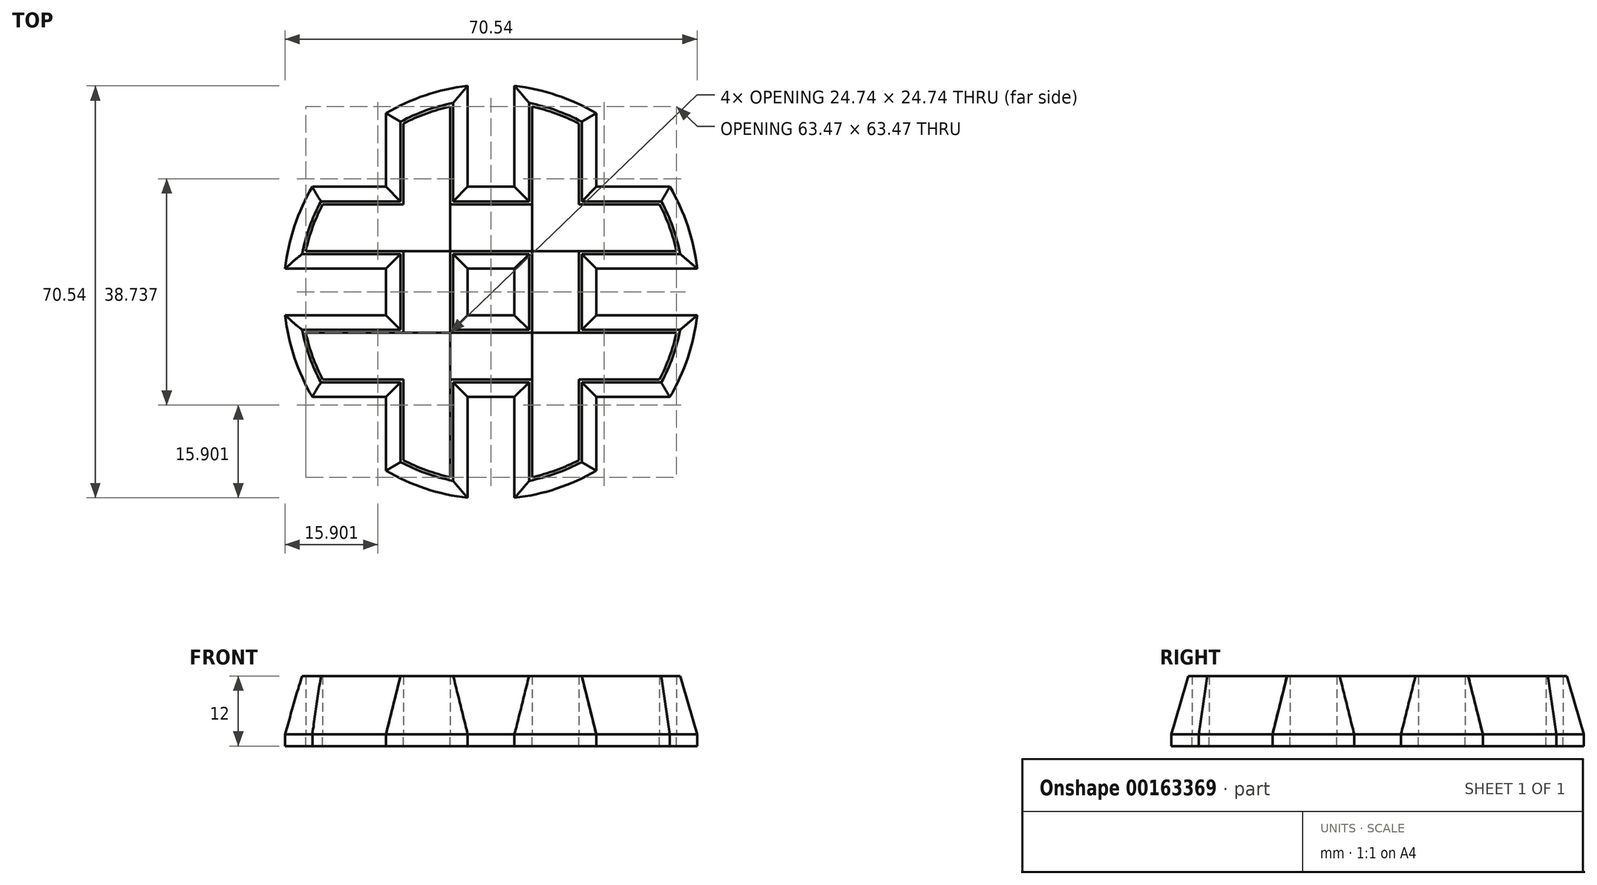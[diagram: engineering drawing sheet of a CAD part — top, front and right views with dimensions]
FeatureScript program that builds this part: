
annotation { "Feature Type Name" : "Feature", "Feature Type Description" : "" }
export const myFeature = defineFeature(function(context is Context, id is Id, definition is map)
    precondition{}
    {
        {
            var Q0;
            Q0=qCreatedBy(makeId("Top.planeOp"),FACE);
            var sketch = newSketch(context, id + "F0", { "sketchPlane" : qUnion([Q0])});
            skArc(sketch, "E0", {"start": v(-28.83, 15) * mm, "mid": v(-30.55, 11.1) * mm, "end": v(-31.74, 7) * mm});
            skLineSegment(sketch, "E1", {"start": v(-28.83, 15) * mm, "end": v(-15, 15) * mm});
            skLineSegment(sketch, "E2", {"start": v(-31.74, 7) * mm, "end": v(-15, 7) * mm});
            skLineSegment(sketch, "E3", {"start": v(-28.83, -15) * mm, "end": v(-15, -15) * mm});
            skLineSegment(sketch, "E4", {"start": v(31.74, -7) * mm, "end": v(15, -7) * mm});
            skLineSegment(sketch, "E5", {"start": v(15, 28.83) * mm, "end": v(15, 15) * mm});
            skLineSegment(sketch, "E6", {"start": v(7, -31.74) * mm, "end": v(7, -15) * mm});
            skLineSegment(sketch, "E7", {"start": v(-15, 28.83) * mm, "end": v(-15, 15) * mm});
            skLineSegment(sketch, "E8", {"start": v(-7, 31.74) * mm, "end": v(-7, 15) * mm});
            skArc(sketch, "E9.trimOffspring", {"start": v(15, 28.83) * mm, "mid": v(11.1, 30.55) * mm, "end": v(7, 31.74) * mm});
            skArc(sketch, "E10.trimOffspring", {"start": v(-31.74, -7) * mm, "mid": v(-30.55, -11.1) * mm, "end": v(-28.83, -15) * mm});
            skArc(sketch, "E11.trimOffspring", {"start": v(-15, -28.83) * mm, "mid": v(-11.1, -30.55) * mm, "end": v(-7, -31.74) * mm});
            skArc(sketch, "E12.trimOffspring", {"start": v(7, -31.74) * mm, "mid": v(11.1, -30.55) * mm, "end": v(15, -28.83) * mm});
            skArc(sketch, "E13.trimOffspring", {"start": v(28.83, -15) * mm, "mid": v(30.55, -11.1) * mm, "end": v(31.74, -7) * mm});
            skArc(sketch, "E14.trimOffspring", {"start": v(31.74, 7) * mm, "mid": v(30.55, 11.1) * mm, "end": v(28.83, 15) * mm});
            skArc(sketch, "E15.trimOffspring", {"start": v(-7, 31.74) * mm, "mid": v(-11.1, 30.55) * mm, "end": v(-15, 28.83) * mm});
            skLineSegment(sketch, "E16.trimOffspring", {"start": v(-7, -15) * mm, "end": v(-7, -31.74) * mm});
            skLineSegment(sketch, "E17.trimOffspring", {"start": v(-15, -7) * mm, "end": v(-31.74, -7) * mm});
            skLineSegment(sketch, "E18.trimOffspring", {"start": v(-15, -15) * mm, "end": v(-15, -28.83) * mm});
            skLineSegment(sketch, "E19.trimOffspring", {"start": v(-7, -15) * mm, "end": v(7, -15) * mm});
            skLineSegment(sketch, "E20.trimOffspring", {"start": v(15, -15) * mm, "end": v(28.83, -15) * mm});
            skLineSegment(sketch, "E21.trimOffspring", {"start": v(7, -7) * mm, "end": v(7, 7) * mm});
            skLineSegment(sketch, "E22.trimOffspring", {"start": v(15, -15) * mm, "end": v(15, -28.83) * mm});
            skLineSegment(sketch, "E23.trimOffspring", {"start": v(7, -7) * mm, "end": v(-7, -7) * mm});
            skLineSegment(sketch, "E24.trimOffspring", {"start": v(15, 7) * mm, "end": v(31.74, 7) * mm});
            skLineSegment(sketch, "E25.trimOffspring", {"start": v(15, 15) * mm, "end": v(28.83, 15) * mm});
            skLineSegment(sketch, "E26.trimOffspring", {"start": v(7, 15) * mm, "end": v(7, 31.74) * mm});
            skLineSegment(sketch, "E27.trimOffspring", {"start": v(15, 7) * mm, "end": v(15, -7) * mm});
            skLineSegment(sketch, "E28.trimOffspring", {"start": v(-7, 7) * mm, "end": v(-7, -7) * mm});
            skLineSegment(sketch, "E29.trimOffspring", {"start": v(-7, 7) * mm, "end": v(7, 7) * mm});
            skLineSegment(sketch, "E30.trimOffspring", {"start": v(-15, 7) * mm, "end": v(-15, -7) * mm});
            skLineSegment(sketch, "E31.trimOffspring", {"start": v(-7, 15) * mm, "end": v(7, 15) * mm});
            skLineSegment(sketch, "E32.0", {"start": v(-35.27, 4) * mm, "end": v(-18, 4) * mm});
            skArc(sketch, "E32.1", {"start": v(-30.6, 18) * mm, "mid": v(-33.67, 11.25) * mm, "end": v(-35.27, 4) * mm});
            skLineSegment(sketch, "E32.2", {"start": v(-30.6, 18) * mm, "end": v(-18, 18) * mm});
            skLineSegment(sketch, "E32.3", {"start": v(-18, 30.6) * mm, "end": v(-18, 18) * mm});
            skArc(sketch, "E32.4", {"start": v(-4, 35.27) * mm, "mid": v(-11.25, 33.67) * mm, "end": v(-18, 30.6) * mm});
            skLineSegment(sketch, "E32.5", {"start": v(18, -18) * mm, "end": v(18, -30.6) * mm});
            skArc(sketch, "E32.6", {"start": v(4, -35.27) * mm, "mid": v(11.25, -33.67) * mm, "end": v(18, -30.6) * mm});
            skLineSegment(sketch, "E32.7", {"start": v(4, -35.27) * mm, "end": v(4, -18) * mm});
            skLineSegment(sketch, "E32.8", {"start": v(-4, -18) * mm, "end": v(4, -18) * mm});
            skLineSegment(sketch, "E32.9", {"start": v(-4, -18) * mm, "end": v(-4, -35.27) * mm});
            skArc(sketch, "E32.10", {"start": v(-18, -30.6) * mm, "mid": v(-11.25, -33.67) * mm, "end": v(-4, -35.27) * mm});
            skLineSegment(sketch, "E32.11", {"start": v(-18, -4) * mm, "end": v(-35.27, -4) * mm});
            skArc(sketch, "E32.12", {"start": v(-35.27, -4) * mm, "mid": v(-33.67, -11.25) * mm, "end": v(-30.6, -18) * mm});
            skLineSegment(sketch, "E32.13", {"start": v(-30.6, -18) * mm, "end": v(-18, -18) * mm});
            skLineSegment(sketch, "E32.14", {"start": v(-18, -18) * mm, "end": v(-18, -30.6) * mm});
            skLineSegment(sketch, "E32.15", {"start": v(18, -18) * mm, "end": v(30.6, -18) * mm});
            skArc(sketch, "E32.16", {"start": v(30.6, -18) * mm, "mid": v(33.67, -11.25) * mm, "end": v(35.27, -4) * mm});
            skLineSegment(sketch, "E32.17", {"start": v(35.27, -4) * mm, "end": v(18, -4) * mm});
            skLineSegment(sketch, "E32.18", {"start": v(18, 4) * mm, "end": v(18, -4) * mm});
            skLineSegment(sketch, "E32.19", {"start": v(18, 4) * mm, "end": v(35.27, 4) * mm});
            skLineSegment(sketch, "E32.20", {"start": v(-18, 4) * mm, "end": v(-18, -4) * mm});
            skArc(sketch, "E32.21", {"start": v(35.27, 4) * mm, "mid": v(33.67, 11.25) * mm, "end": v(30.6, 18) * mm});
            skLineSegment(sketch, "E32.22", {"start": v(18, 18) * mm, "end": v(30.6, 18) * mm});
            skLineSegment(sketch, "E32.23", {"start": v(18, 30.6) * mm, "end": v(18, 18) * mm});
            skArc(sketch, "E32.24", {"start": v(18, 30.6) * mm, "mid": v(11.25, 33.67) * mm, "end": v(4, 35.27) * mm});
            skLineSegment(sketch, "E32.25", {"start": v(4, 18) * mm, "end": v(4, 35.27) * mm});
            skLineSegment(sketch, "E32.26", {"start": v(-4, 18) * mm, "end": v(4, 18) * mm});
            skLineSegment(sketch, "E32.27", {"start": v(-4, 35.27) * mm, "end": v(-4, 18) * mm});
            skLineSegment(sketch, "E33.0", {"start": v(4, -4) * mm, "end": v(-4, -4) * mm});
            skLineSegment(sketch, "E33.1", {"start": v(4, -4) * mm, "end": v(4, 4) * mm});
            skLineSegment(sketch, "E33.2", {"start": v(-4, 4) * mm, "end": v(4, 4) * mm});
            skLineSegment(sketch, "E33.3", {"start": v(-4, 4) * mm, "end": v(-4, -4) * mm});
            skSolve(sketch);
        }
        {
            var Q0;
            {var subQ0=sQuery(id+"F0.wireOp",EDGE,"E7");var subQ1=sQuery(id+"F0.wireOp",EDGE,"E2");var subQ2=makeQuery(id+"F0.imprint","INTERSECT",VERTEX,{"derivedFrom":[subQ1,subQ0]});Q0=makeQuery(id+"F0.imprint","IMPRINT",FACE,{"disambiguationData":[TD([[makeQuery(id+"F0.imprint","IMPRINT",EDGE,{"disambiguationData":[TD([[subQ2,-1.0]])],"derivedFrom":subQ1}),-1.0]])]});}
            var Q1;
            Q1=makeQuery(id+"F0.imprint","IMPRINT",FACE,{"disambiguationData":[TD([[makeQuery(id+"F0.imprint","IMPRINT",EDGE,{"derivedFrom":sQuery(id+"F0.wireOp",EDGE,"E21.trimOffspring")}),1.0]])]});
            extrude(context, id + "F1", {"entities" : qUnion([Q0, Q1]), "depth" : 10 * mm});
        }
        {
            var Q0;
            Q0=makeQuery(id+"F1.opExtrude","CAP_EDGE",EDGE,{"disambiguationData":[OSD([sQuery(id+"F0.wireOp",EDGE,"E32.17")])],"isStart":false});
            var Q1;
            Q1=makeQuery(id+"F1.opExtrude","CAP_EDGE",EDGE,{"disambiguationData":[OSD([sQuery(id+"F0.wireOp",EDGE,"E32.16")])],"isStart":false});
            var Q2;
            Q2=makeQuery(id+"F1.opExtrude","CAP_EDGE",EDGE,{"disambiguationData":[OSD([sQuery(id+"F0.wireOp",EDGE,"E32.15")])],"isStart":false});
            var Q3;
            Q3=makeQuery(id+"F1.opExtrude","CAP_EDGE",EDGE,{"disambiguationData":[OSD([sQuery(id+"F0.wireOp",EDGE,"E32.5")])],"isStart":false});
            var Q4;
            Q4=makeQuery(id+"F1.opExtrude","CAP_EDGE",EDGE,{"disambiguationData":[OSD([sQuery(id+"F0.wireOp",EDGE,"E32.6")])],"isStart":false});
            var Q5;
            Q5=makeQuery(id+"F1.opExtrude","CAP_EDGE",EDGE,{"disambiguationData":[OSD([sQuery(id+"F0.wireOp",EDGE,"E32.7")])],"isStart":false});
            var Q6;
            Q6=makeQuery(id+"F1.opExtrude","CAP_EDGE",EDGE,{"disambiguationData":[OSD([sQuery(id+"F0.wireOp",EDGE,"E32.9")])],"isStart":false});
            var Q7;
            Q7=makeQuery(id+"F1.opExtrude","CAP_EDGE",EDGE,{"disambiguationData":[OSD([sQuery(id+"F0.wireOp",EDGE,"E32.10")])],"isStart":false});
            var Q8;
            Q8=makeQuery(id+"F1.opExtrude","CAP_EDGE",EDGE,{"disambiguationData":[OSD([sQuery(id+"F0.wireOp",EDGE,"E32.14")])],"isStart":false});
            var Q9;
            Q9=makeQuery(id+"F1.opExtrude","CAP_EDGE",EDGE,{"disambiguationData":[OSD([sQuery(id+"F0.wireOp",EDGE,"E32.13")])],"isStart":false});
            var Q10;
            Q10=makeQuery(id+"F1.opExtrude","CAP_EDGE",EDGE,{"disambiguationData":[OSD([sQuery(id+"F0.wireOp",EDGE,"E32.12")])],"isStart":false});
            var Q11;
            Q11=makeQuery(id+"F1.opExtrude","CAP_EDGE",EDGE,{"disambiguationData":[OSD([sQuery(id+"F0.wireOp",EDGE,"E32.11")])],"isStart":false});
            var Q12;
            Q12=makeQuery(id+"F1.opExtrude","CAP_EDGE",EDGE,{"disambiguationData":[OSD([sQuery(id+"F0.wireOp",EDGE,"E32.20")])],"isStart":false});
            var Q13;
            Q13=makeQuery(id+"F1.opExtrude","CAP_EDGE",EDGE,{"disambiguationData":[OSD([sQuery(id+"F0.wireOp",EDGE,"E32.0")])],"isStart":false});
            var Q14;
            Q14=makeQuery(id+"F1.opExtrude","CAP_EDGE",EDGE,{"disambiguationData":[OSD([sQuery(id+"F0.wireOp",EDGE,"E32.1")])],"isStart":false});
            var Q15;
            Q15=makeQuery(id+"F1.opExtrude","CAP_EDGE",EDGE,{"disambiguationData":[OSD([sQuery(id+"F0.wireOp",EDGE,"E32.2")])],"isStart":false});
            var Q16;
            Q16=makeQuery(id+"F1.opExtrude","CAP_EDGE",EDGE,{"disambiguationData":[OSD([sQuery(id+"F0.wireOp",EDGE,"E32.3")])],"isStart":false});
            var Q17;
            Q17=makeQuery(id+"F1.opExtrude","CAP_EDGE",EDGE,{"disambiguationData":[OSD([sQuery(id+"F0.wireOp",EDGE,"E32.4")])],"isStart":false});
            var Q18;
            Q18=makeQuery(id+"F1.opExtrude","CAP_EDGE",EDGE,{"disambiguationData":[OSD([sQuery(id+"F0.wireOp",EDGE,"E32.27")])],"isStart":false});
            var Q19;
            Q19=makeQuery(id+"F1.opExtrude","CAP_EDGE",EDGE,{"disambiguationData":[OSD([sQuery(id+"F0.wireOp",EDGE,"E32.26")])],"isStart":false});
            var Q20;
            Q20=makeQuery(id+"F1.opExtrude","CAP_EDGE",EDGE,{"disambiguationData":[OSD([sQuery(id+"F0.wireOp",EDGE,"E32.25")])],"isStart":false});
            var Q21;
            Q21=makeQuery(id+"F1.opExtrude","CAP_EDGE",EDGE,{"disambiguationData":[OSD([sQuery(id+"F0.wireOp",EDGE,"E32.24")])],"isStart":false});
            var Q22;
            Q22=makeQuery(id+"F1.opExtrude","CAP_EDGE",EDGE,{"disambiguationData":[OSD([sQuery(id+"F0.wireOp",EDGE,"E32.23")])],"isStart":false});
            var Q23;
            Q23=makeQuery(id+"F1.opExtrude","CAP_EDGE",EDGE,{"disambiguationData":[OSD([sQuery(id+"F0.wireOp",EDGE,"E32.22")])],"isStart":false});
            var Q24;
            Q24=makeQuery(id+"F1.opExtrude","CAP_EDGE",EDGE,{"disambiguationData":[OSD([sQuery(id+"F0.wireOp",EDGE,"E32.21")])],"isStart":false});
            var Q25;
            Q25=makeQuery(id+"F1.opExtrude","CAP_EDGE",EDGE,{"disambiguationData":[OSD([sQuery(id+"F0.wireOp",EDGE,"E32.19")])],"isStart":false});
            var Q26;
            Q26=makeQuery(id+"F1.opExtrude","CAP_EDGE",EDGE,{"disambiguationData":[OSD([sQuery(id+"F0.wireOp",EDGE,"E32.18")])],"isStart":false});
            var Q27;
            Q27=makeQuery(id+"F1.opExtrude","CAP_EDGE",EDGE,{"disambiguationData":[OSD([sQuery(id+"F0.wireOp",EDGE,"E32.8")])],"isStart":false});
            chamfer(context, id + "F2", {"entities" : qUnion([Q0, Q1, Q2, Q3, Q4, Q5, Q6, Q7, Q8, Q9, Q10, Q11, Q12, Q13, Q14, Q15, Q16, Q17, Q18, Q19, Q20, Q21, Q22, Q23, Q24, Q25, Q26, Q27]), "chamferType" : ChamferType.OFFSET_ANGLE, "width" : 10 * mm, "oppositeDirection" : true, "angle" : 14 * degree, "tangentPropagation" : true});
        }
        {
            var Q0;
            Q0=makeQuery(id+"F1.opExtrude","CAP_EDGE",EDGE,{"disambiguationData":[OSD([sQuery(id+"F0.wireOp",EDGE,"E33.1")])],"isStart":false});
            var Q1;
            Q1=makeQuery(id+"F1.opExtrude","CAP_EDGE",EDGE,{"disambiguationData":[OSD([sQuery(id+"F0.wireOp",EDGE,"E33.0")])],"isStart":false});
            var Q2;
            Q2=makeQuery(id+"F1.opExtrude","CAP_EDGE",EDGE,{"disambiguationData":[OSD([sQuery(id+"F0.wireOp",EDGE,"E33.3")])],"isStart":false});
            var Q3;
            Q3=makeQuery(id+"F1.opExtrude","CAP_EDGE",EDGE,{"disambiguationData":[OSD([sQuery(id+"F0.wireOp",EDGE,"E33.2")])],"isStart":false});
            chamfer(context, id + "F3", {"entities" : qUnion([Q0, Q1, Q2, Q3]), "chamferType" : ChamferType.OFFSET_ANGLE, "width" : 10 * mm, "oppositeDirection" : false, "angle" : 14 * degree, "tangentPropagation" : true});
        }
        {
            var Q0;
            Q0=makeQuery(id+"F0.imprint","IMPRINT",FACE,{"disambiguationData":[TD([[makeQuery(id+"F0.imprint","IMPRINT",EDGE,{"derivedFrom":sQuery(id+"F0.wireOp",EDGE,"E0")}),-1.0]])]});
            var sketch = newSketch(context, id + "F4", { "sketchPlane" : qUnion([Q0])});
            skPoint(sketch, "E34.0", {"position": v(7, -23.37) * mm});
            skLineSegment(sketch, "E35.0", {"start": v(-18, 4) * mm, "end": v(-18, -4) * mm});
            skLineSegment(sketch, "E36.0", {"start": v(-4, 18) * mm, "end": v(4, 18) * mm});
            skLineSegment(sketch, "E37.0", {"start": v(18, 4) * mm, "end": v(18, -4) * mm});
            skLineSegment(sketch, "E38.0", {"start": v(-4, -18) * mm, "end": v(4, -18) * mm});
            skLineSegment(sketch, "E39.0", {"start": v(4, -4) * mm, "end": v(-4, -4) * mm});
            skLineSegment(sketch, "E40.0", {"start": v(-4, 4) * mm, "end": v(-4, -4) * mm});
            skLineSegment(sketch, "E41.0", {"start": v(-4, 4) * mm, "end": v(4, 4) * mm});
            skLineSegment(sketch, "E42.0", {"start": v(4, -4) * mm, "end": v(4, 4) * mm});
            skPoint(sketch, "E43.orphan", {"position": v(-7, 15) * mm});
            skPoint(sketch, "E44.orphan", {"position": v(-15, 7) * mm});
            skPoint(sketch, "E45.orphan", {"position": v(-15, -7) * mm});
            skPoint(sketch, "E46.orphan", {"position": v(-7, -15) * mm});
            skPoint(sketch, "E47.orphan", {"position": v(7, -15) * mm});
            skPoint(sketch, "E48.orphan", {"position": v(15, -7) * mm});
            skPoint(sketch, "E49.orphan", {"position": v(15, 7) * mm});
            skPoint(sketch, "E50.orphan", {"position": v(7, 15) * mm});
            skPoint(sketch, "E51.orphan", {"position": v(-4, 18) * mm});
            skPoint(sketch, "E52.orphan", {"position": v(4, 18) * mm});
            skPoint(sketch, "E53.orphan", {"position": v(18, -4) * mm});
            skPoint(sketch, "E54.orphan", {"position": v(4, -18) * mm});
            skPoint(sketch, "E55.orphan", {"position": v(18, 4) * mm});
            skPoint(sketch, "E56.orphan", {"position": v(-4, -18) * mm});
            skPoint(sketch, "E57.orphan", {"position": v(-18, -4) * mm});
            skPoint(sketch, "E58.orphan", {"position": v(-18, 4) * mm});
            skLineSegment(sketch, "E59.0", {"start": v(-4, 35.27) * mm, "end": v(-4, 18) * mm});
            skLineSegment(sketch, "E60.0", {"start": v(4, 18) * mm, "end": v(4, 35.27) * mm});
            skArc(sketch, "E61.0", {"start": v(18, 30.6) * mm, "mid": v(11.25, 33.67) * mm, "end": v(4, 35.27) * mm});
            skLineSegment(sketch, "E62.0", {"start": v(18, 30.6) * mm, "end": v(18, 18) * mm});
            skPoint(sketch, "E63.0", {"position": v(24.3, 18) * mm});
            skLineSegment(sketch, "E64.0", {"start": v(18, 18) * mm, "end": v(30.6, 18) * mm});
            skArc(sketch, "E65.0", {"start": v(35.27, 4) * mm, "mid": v(33.67, 11.25) * mm, "end": v(30.6, 18) * mm});
            skLineSegment(sketch, "E66.0", {"start": v(18, 4) * mm, "end": v(35.27, 4) * mm});
            skLineSegment(sketch, "E67.0", {"start": v(35.27, -4) * mm, "end": v(18, -4) * mm});
            skPoint(sketch, "E68.0", {"position": v(33.67, -11.25) * mm});
            skLineSegment(sketch, "E69.0", {"start": v(18, -18) * mm, "end": v(30.6, -18) * mm});
            skLineSegment(sketch, "E70.0", {"start": v(18, -18) * mm, "end": v(18, -30.6) * mm});
            skArc(sketch, "E71.0", {"start": v(4, -35.27) * mm, "mid": v(11.25, -33.67) * mm, "end": v(18, -30.6) * mm});
            skLineSegment(sketch, "E72.0", {"start": v(4, -35.27) * mm, "end": v(4, -18) * mm});
            skLineSegment(sketch, "E73.0", {"start": v(-4, -18) * mm, "end": v(-4, -35.27) * mm});
            skPoint(sketch, "E74.0", {"position": v(-11.25, -33.67) * mm});
            skArc(sketch, "E75.0", {"start": v(-18, -30.6) * mm, "mid": v(-11.25, -33.67) * mm, "end": v(-4, -35.27) * mm});
            skLineSegment(sketch, "E76.0", {"start": v(-18, -18) * mm, "end": v(-18, -30.6) * mm});
            skLineSegment(sketch, "E77.0", {"start": v(-30.6, -18) * mm, "end": v(-18, -18) * mm});
            skArc(sketch, "E78.0", {"start": v(-35.27, -4) * mm, "mid": v(-33.67, -11.25) * mm, "end": v(-30.6, -18) * mm});
            skLineSegment(sketch, "E79.0", {"start": v(-18, -4) * mm, "end": v(-35.27, -4) * mm});
            skLineSegment(sketch, "E80.0", {"start": v(-35.27, 4) * mm, "end": v(-18, 4) * mm});
            skArc(sketch, "E81.0", {"start": v(-30.6, 18) * mm, "mid": v(-33.67, 11.25) * mm, "end": v(-35.27, 4) * mm});
            skPoint(sketch, "E82.0", {"position": v(-24.3, 18) * mm});
            skLineSegment(sketch, "E83.0", {"start": v(-30.6, 18) * mm, "end": v(-18, 18) * mm});
            skLineSegment(sketch, "E84.0", {"start": v(-18, 30.6) * mm, "end": v(-18, 18) * mm});
            skPoint(sketch, "E85.orphan", {"position": v(-7, -31.74) * mm});
            skPoint(sketch, "E86.orphan", {"position": v(7, -31.74) * mm});
            skPoint(sketch, "E87.orphan", {"position": v(31.74, -7) * mm});
            skPoint(sketch, "E88.orphan", {"position": v(31.74, 7) * mm});
            skPoint(sketch, "E89.orphan", {"position": v(7, 31.74) * mm});
            skPoint(sketch, "E90.orphan", {"position": v(-7, 31.74) * mm});
            skArc(sketch, "E91.0", {"start": v(-4, 35.27) * mm, "mid": v(-11.25, 33.67) * mm, "end": v(-18, 30.6) * mm});
            skLineSegment(sketch, "E92.0", {"start": v(-7, 31.74) * mm, "end": v(-7, 7) * mm});
            skArc(sketch, "E93.0", {"start": v(-7, 31.74) * mm, "mid": v(-11.1, 30.55) * mm, "end": v(-15, 28.83) * mm});
            skLineSegment(sketch, "E94.0", {"start": v(-15, 28.83) * mm, "end": v(-15, 15) * mm});
            skLineSegment(sketch, "E95.0", {"start": v(-28.83, 15) * mm, "end": v(-15, 15) * mm});
            skPoint(sketch, "E96.0", {"position": v(-30.55, 11.1) * mm});
            skArc(sketch, "E97.0", {"start": v(-28.83, 15) * mm, "mid": v(-30.55, 11.1) * mm, "end": v(-31.74, 7) * mm});
            skArc(sketch, "E98.0", {"start": v(-31.74, -7) * mm, "mid": v(-30.55, -11.1) * mm, "end": v(-28.83, -15) * mm});
            skLineSegment(sketch, "E99.0", {"start": v(-28.83, -15) * mm, "end": v(-15, -15) * mm});
            skLineSegment(sketch, "E100.0", {"start": v(-15, -15) * mm, "end": v(-15, -28.83) * mm});
            skArc(sketch, "E101.0", {"start": v(-15, -28.83) * mm, "mid": v(-11.1, -30.55) * mm, "end": v(-7, -31.74) * mm});
            skLineSegment(sketch, "E102.0", {"start": v(-7, -15) * mm, "end": v(-7, -31.74) * mm});
            skLineSegment(sketch, "E103.0", {"start": v(7, -31.74) * mm, "end": v(7, -15) * mm});
            skArc(sketch, "E104.0", {"start": v(7, -31.74) * mm, "mid": v(11.1, -30.55) * mm, "end": v(15, -28.83) * mm});
            skLineSegment(sketch, "E105.0", {"start": v(15, -15) * mm, "end": v(15, -28.83) * mm});
            skLineSegment(sketch, "E106.0", {"start": v(15, -15) * mm, "end": v(28.83, -15) * mm});
            skArc(sketch, "E107.0", {"start": v(28.83, -15) * mm, "mid": v(30.55, -11.1) * mm, "end": v(31.74, -7) * mm});
            skLineSegment(sketch, "E108.0", {"start": v(31.74, -7) * mm, "end": v(7, -7) * mm});
            skLineSegment(sketch, "E109.0", {"start": v(7, 7) * mm, "end": v(31.74, 7) * mm});
            skArc(sketch, "E110.0", {"start": v(31.74, 7) * mm, "mid": v(30.55, 11.1) * mm, "end": v(28.83, 15) * mm});
            skLineSegment(sketch, "E111.0", {"start": v(15, 15) * mm, "end": v(28.83, 15) * mm});
            skLineSegment(sketch, "E112.0", {"start": v(15, 28.83) * mm, "end": v(15, 15) * mm});
            skArc(sketch, "E113.0", {"start": v(15, 28.83) * mm, "mid": v(11.1, 30.55) * mm, "end": v(7, 31.74) * mm});
            skLineSegment(sketch, "E114.0.0", {"start": v(-15, 15) * mm, "end": v(-28.83, 15) * mm});
            skLineSegment(sketch, "E114.0.2", {"start": v(-31.74, 7) * mm, "end": v(-7, 7) * mm});
            skLineSegment(sketch, "E114.0.4", {"start": v(-7, -7) * mm, "end": v(-31.74, -7) * mm});
            skLineSegment(sketch, "E114.0.9", {"start": v(-7, -31.74) * mm, "end": v(-7, -7) * mm});
            skLineSegment(sketch, "E114.0.11", {"start": v(7, -7) * mm, "end": v(7, -31.74) * mm});
            skLineSegment(sketch, "E114.0.13", {"start": v(15, -28.83) * mm, "end": v(15, -15) * mm});
            skLineSegment(sketch, "E114.0.16", {"start": v(31.74, -7) * mm, "end": v(15, -7) * mm});
            skLineSegment(sketch, "E114.0.18", {"start": v(15, 7) * mm, "end": v(31.74, 7) * mm});
            skLineSegment(sketch, "E114.0.20", {"start": v(28.83, 15) * mm, "end": v(15, 15) * mm});
            skLineSegment(sketch, "E114.0.21", {"start": v(15, 15) * mm, "end": v(15, 28.83) * mm});
            skLineSegment(sketch, "E114.0.23", {"start": v(7, 31.74) * mm, "end": v(7, 7) * mm});
            skLineSegment(sketch, "E114.0.25", {"start": v(-7, 15) * mm, "end": v(-7, 31.74) * mm});
            skSolve(sketch);
        }
        {
            var Q0;
            Q0=makeQuery(id+"F4.imprint","IMPRINT",FACE,{"disambiguationData":[TD([[makeQuery(id+"F4.imprint","IMPRINT",EDGE,{"derivedFrom":sQuery(id+"F4.wireOp",EDGE,"E39.0")}),1.0]])]});
            var Q1;
            Q1=makeQuery(id+"F4.imprint","IMPRINT",FACE,{"disambiguationData":[TD([[makeQuery(id+"F4.imprint","IMPRINT",EDGE,{"derivedFrom":sQuery(id+"F4.wireOp",EDGE,"E35.0")}),1.0]])]});
            extrude(context, id + "F5", {"entities" : qUnion([Q0, Q1]), "oppositeDirection" : true, "depth" : 2 * mm});
        }
    });
